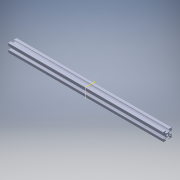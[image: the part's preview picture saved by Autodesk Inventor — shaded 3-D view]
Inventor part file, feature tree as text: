
AUTODESK INVENTOR PART (.ipt)
format: ipt  version: 2018 (Build 220112000, 112)  size: 374,784 bytes
history: native  units: in
note: dims shown in document units (in); Inventor stores cm internally (conversion verified against a paired STEP export)
features: extrude x1, plane x1, sketch x1, projected_geometry x1, fillet x1
ambient origin geometry x8: Origin, YZ Plane, XZ Plane, XY Plane, X Axis, Y Axis, Z Axis, Center Point
bodies: Solid1 (feature_tree)
feature tree (5):
  extrude  "Extrusion2"  [1 undecoded]
  plane  "Work Plane1"
  sketch  "Sketch3"  dims[d2=10.2362in d3=0.0in]
  projected_geometry  "Projected Loop2"
  fillet  "Fillet5"  [1 undecoded]
note: 2 required parameter values undecoded (feature->parameter linkage not recoverable at this tier; creation-order binding heuristic only, values carry confidence <= 0.55)
